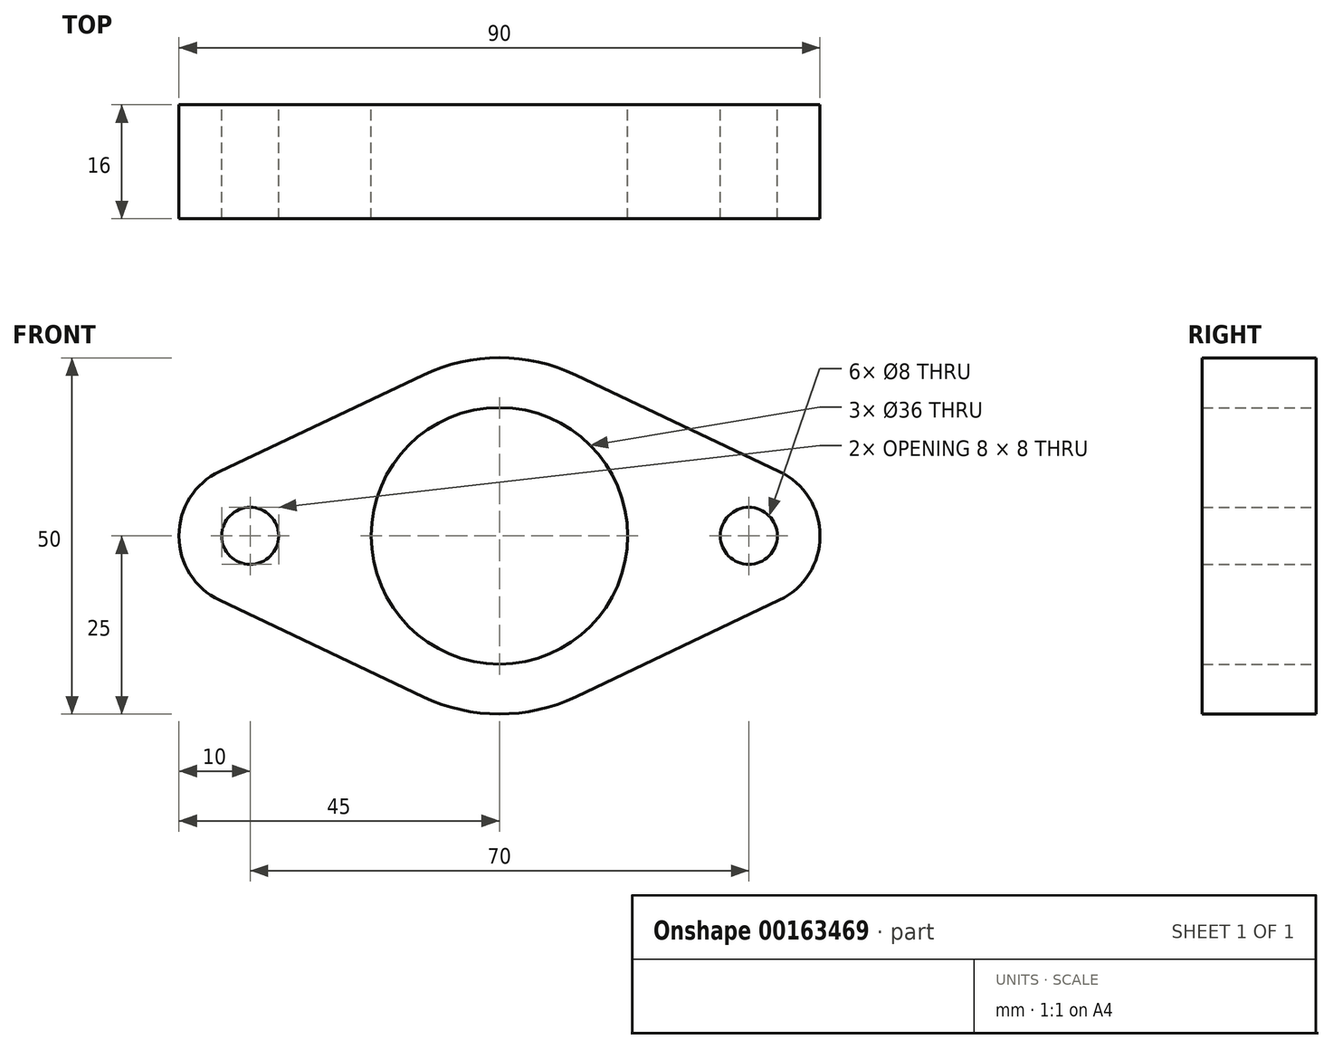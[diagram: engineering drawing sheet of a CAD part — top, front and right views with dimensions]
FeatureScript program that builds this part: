
annotation { "Feature Type Name" : "Feature", "Feature Type Description" : "" }
export const myFeature = defineFeature(function(context is Context, id is Id, definition is map)
    precondition{}
    {
        {
            var Q0;
            Q0=qCreatedBy(makeId("Front.planeOp"),FACE);
            var sketch = newSketch(context, id + "F0", { "sketchPlane" : qUnion([Q0])});
            skCircle(sketch, "E0", {"center": v(0, 0) * mm, "radius": 18 * mm});
            skArc(sketch, "E1", {"start": v(-10.71, -22.59) * mm, "mid": v(0, -25) * mm, "end": v(10.71, -22.59) * mm});
            skLineSegment(sketch, "E2", {"start": v(0, 0) * mm, "end": v(35, 0) * mm, "construction": true});
            skArc(sketch, "E3", {"start": v(39.29, -9.04) * mm, "mid": v(45, 0) * mm, "end": v(39.29, 9.04) * mm});
            skLineSegment(sketch, "E4", {"start": v(0, 0) * mm, "end": v(-35, 0) * mm, "construction": true});
            skArc(sketch, "E5", {"start": v(-39.29, 9.04) * mm, "mid": v(-45, 0) * mm, "end": v(-39.29, -9.04) * mm});
            skLineSegment(sketch, "E6", {"start": v(-39.29, 9.04) * mm, "end": v(-10.71, 22.59) * mm});
            skLineSegment(sketch, "E7", {"start": v(10.71, 22.59) * mm, "end": v(39.29, 9.04) * mm});
            skLineSegment(sketch, "E8", {"start": v(-39.29, -9.04) * mm, "end": v(-10.71, -22.59) * mm});
            skLineSegment(sketch, "E9", {"start": v(10.71, -22.59) * mm, "end": v(39.29, -9.04) * mm});
            skArc(sketch, "E10.trimOffspring", {"start": v(10.71, 22.59) * mm, "mid": v(0, 25) * mm, "end": v(-10.71, 22.59) * mm});
            skSolve(sketch);
        }
        {
            var Q0;
            Q0 = qSketchRegion(id + "F0", true);
            extrude(context, id + "F1", {"entities" : qUnion([Q0]), "depth" : 16 * mm});
        }
        {
            var Q0;
            Q0=sQuery(id+"F0.wireOp",VERTEX,"E3.center");
            var Q1;
            Q1=sQuery(id+"F0.wireOp",VERTEX,"E5.center");
            var Q2;
            Q2=makeQuery(id+"F1.opExtrude","SWEPT_BODY",BODY,{"disambiguationData":[OSD([sQuery(id+"F0.wireOp",EDGE,"E0"),sQuery(id+"F0.wireOp",EDGE,"E1"),sQuery(id+"F0.wireOp",EDGE,"E3"),sQuery(id+"F0.wireOp",EDGE,"E5"),sQuery(id+"F0.wireOp",EDGE,"E6"),sQuery(id+"F0.wireOp",EDGE,"E7"),sQuery(id+"F0.wireOp",EDGE,"E8"),sQuery(id+"F0.wireOp",EDGE,"E9"),sQuery(id+"F0.wireOp",EDGE,"E10.trimOffspring")])]});
            hole(context, id + "F2", {"style" : HoleStyle.SIMPLE, "endStyle" : HoleEndStyle.THROUGH, "oppositeDirection" : true, "holeDiameter" : 8 * mm, "locations" : qUnion([Q0, Q1]), "scope" : qUnion([Q2]), "isTappedThrough" : true});
        }
    });
